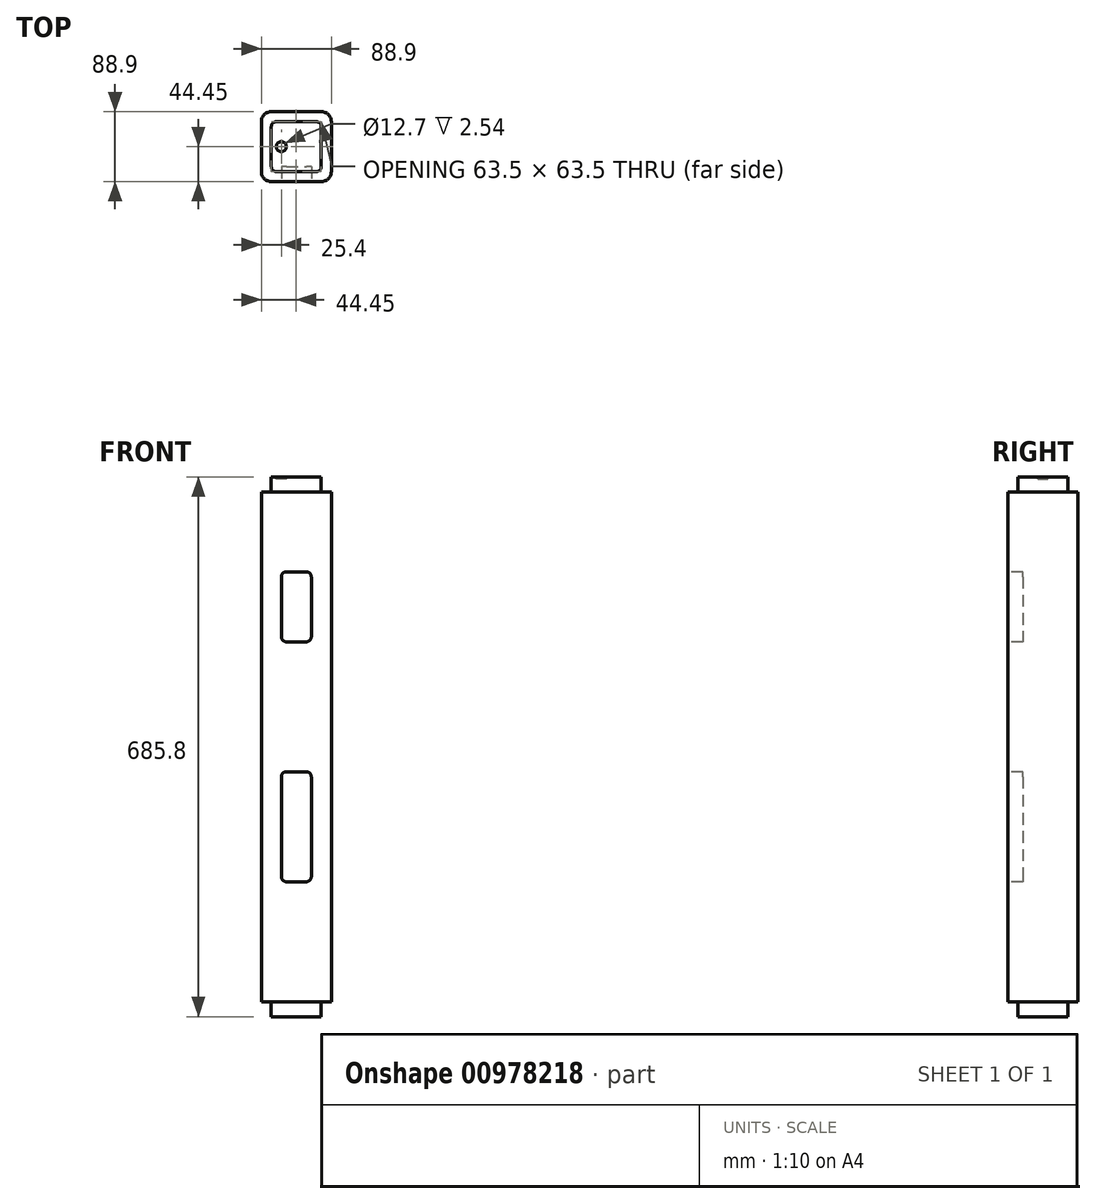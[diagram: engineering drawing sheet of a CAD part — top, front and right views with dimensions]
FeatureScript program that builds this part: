
annotation { "Feature Type Name" : "Feature", "Feature Type Description" : "" }
export const myFeature = defineFeature(function(context is Context, id is Id, definition is map)
    precondition{}
    {
        {
            var Q0;
            Q0=qCreatedBy(makeId("Front.planeOp"),FACE);
            var sketch = newSketch(context, id + "F0", { "sketchPlane" : qUnion([Q0])});
            skLineSegment(sketch, "E0", {"start": v(0, 0) * mm, "end": v(0, 101.9) * mm, "construction": true});
            skSolve(sketch);
        }
        {
            var Q0;
            Q0=qCreatedBy(makeId("Top.planeOp"),FACE);
            var sketch = newSketch(context, id + "F1", { "sketchPlane" : qUnion([Q0])});
            skLineSegment(sketch, "E1", {"start": v(0, 0) * mm, "end": v(0, 44.45) * mm, "construction": true});
            skLineSegment(sketch, "E2", {"start": v(0, 0) * mm, "end": v(-44.45, 0) * mm, "construction": true});
            skLineSegment(sketch, "E3", {"start": v(0, 0) * mm, "end": v(0, -44.45) * mm, "construction": true});
            skLineSegment(sketch, "E4", {"start": v(0, 0) * mm, "end": v(44.45, 0) * mm, "construction": true});
            skLineSegment(sketch, "E5", {"start": v(-44.45, 0) * mm, "end": v(-44.45, 19.05) * mm});
            skLineSegment(sketch, "E6", {"start": v(-44.45, 19.05) * mm, "end": v(-19.05, 19.05) * mm, "construction": true});
            skLineSegment(sketch, "E7", {"start": v(-19.05, 19.05) * mm, "end": v(-19.05, 44.45) * mm, "construction": true});
            skLineSegment(sketch, "E8", {"start": v(0, 44.45) * mm, "end": v(-19.05, 44.45) * mm});
            skLineSegment(sketch, "E9", {"start": v(-44.45, 0) * mm, "end": v(-44.45, -19.05) * mm});
            skLineSegment(sketch, "E10", {"start": v(-44.45, -19.05) * mm, "end": v(-19.05, -19.05) * mm, "construction": true});
            skLineSegment(sketch, "E11", {"start": v(-19.05, -19.05) * mm, "end": v(-19.05, -44.45) * mm, "construction": true});
            skLineSegment(sketch, "E12", {"start": v(-19.05, -44.45) * mm, "end": v(0, -44.45) * mm});
            skLineSegment(sketch, "E13", {"start": v(0, 44.45) * mm, "end": v(19.05, 44.45) * mm});
            skLineSegment(sketch, "E14", {"start": v(19.05, 44.45) * mm, "end": v(19.05, 19.05) * mm, "construction": true});
            skLineSegment(sketch, "E15", {"start": v(19.05, 19.05) * mm, "end": v(44.45, 19.05) * mm, "construction": true});
            skLineSegment(sketch, "E16", {"start": v(44.45, 0) * mm, "end": v(44.45, 19.05) * mm});
            skLineSegment(sketch, "E17", {"start": v(44.45, 0) * mm, "end": v(44.45, -19.05) * mm});
            skLineSegment(sketch, "E18", {"start": v(44.45, -19.05) * mm, "end": v(19.05, -19.05) * mm, "construction": true});
            skLineSegment(sketch, "E19", {"start": v(19.05, -19.05) * mm, "end": v(19.05, -44.45) * mm, "construction": true});
            skLineSegment(sketch, "E20", {"start": v(0, -44.45) * mm, "end": v(19.05, -44.45) * mm});
            skLineSegment(sketch, "E21", {"start": v(44.45, -19.05) * mm, "end": v(44.45, -44.45) * mm});
            skLineSegment(sketch, "E22", {"start": v(19.05, -44.45) * mm, "end": v(44.45, -44.45) * mm});
            skLineSegment(sketch, "E23", {"start": v(-19.05, -44.45) * mm, "end": v(-44.45, -44.45) * mm});
            skLineSegment(sketch, "E24", {"start": v(-44.45, -19.05) * mm, "end": v(-44.45, -44.45) * mm});
            skLineSegment(sketch, "E25", {"start": v(44.45, 19.05) * mm, "end": v(44.45, 44.45) * mm});
            skLineSegment(sketch, "E26", {"start": v(19.05, 44.45) * mm, "end": v(44.45, 44.45) * mm});
            skLineSegment(sketch, "E27", {"start": v(-19.05, 44.45) * mm, "end": v(-44.45, 44.45) * mm});
            skLineSegment(sketch, "E28", {"start": v(-44.45, 19.05) * mm, "end": v(-44.45, 44.45) * mm});
            skSolve(sketch);
        }
        {
            var Q0;
            Q0=makeQuery(id+"F1.imprint","IMPRINT",FACE,{"disambiguationData":[TD([[makeQuery(id+"F1.imprint","IMPRINT",EDGE,{"derivedFrom":sQuery(id+"F1.wireOp",EDGE,"E5")}),-1.0]])]});
            extrude(context, id + "F2", {"entities" : qUnion([Q0]), "oppositeDirection" : true, "depth" : 647.7 * mm, "offsetDistance" : 25.4 * mm});
        }
        {
            var Q0;
            Q0=makeQuery(id+"F2.opExtrude","SWEPT_FACE",FACE,{"disambiguationData":[OSD([sQuery(id+"F1.wireOp",EDGE,"E12"),sQuery(id+"F1.wireOp",EDGE,"E20")])]});
            var sketch = newSketch(context, id + "F3", { "sketchPlane" : qUnion([Q0])});
            skLineSegment(sketch, "E29.bottom", {"start": v(-19.05, -101.6) * mm, "end": v(19.05, -101.6) * mm});
            skLineSegment(sketch, "E29.top", {"start": v(-19.05, -190.5) * mm, "end": v(19.05, -190.5) * mm});
            skLineSegment(sketch, "E29.left", {"start": v(-19.05, -101.6) * mm, "end": v(-19.05, -190.5) * mm});
            skLineSegment(sketch, "E29.right", {"start": v(19.05, -101.6) * mm, "end": v(19.05, -190.5) * mm});
            skLineSegment(sketch, "E30", {"start": v(0, -190.5) * mm, "end": v(0, -647.7) * mm});
            skSolve(sketch);
        }
        {
            var Q0;
            Q0=makeQuery(id+"F3.imprint","IMPRINT",FACE,{"disambiguationData":[TD([[makeQuery(id+"F3.imprint","IMPRINT",EDGE,{"derivedFrom":sQuery(id+"F3.wireOp",EDGE,"E29.bottom")}),-1.0]])]});
            extrude(context, id + "F4", {"entities" : qUnion([Q0]), "operationType" : NewBodyOperationType.REMOVE, "oppositeDirection" : true, "depth" : 19.05 * mm, "offsetDistance" : 25.4 * mm});
        }
        {
            var Q0;
            Q0=makeQuery(id+"F2.opExtrude","SWEPT_EDGE",EDGE,{"disambiguationData":[OSD([sQuery(id+"F1.wireOp",EDGE,"E23"),sQuery(id+"F1.wireOp",EDGE,"E24")])]});
            var Q1;
            Q1=makeQuery(id+"F2.opExtrude","SWEPT_EDGE",EDGE,{"disambiguationData":[OSD([sQuery(id+"F1.wireOp",EDGE,"E21"),sQuery(id+"F1.wireOp",EDGE,"E22")])]});
            var Q2;
            Q2=makeQuery(id+"F2.opExtrude","SWEPT_EDGE",EDGE,{"disambiguationData":[OSD([sQuery(id+"F1.wireOp",EDGE,"E25"),sQuery(id+"F1.wireOp",EDGE,"E26")])]});
            var Q3;
            Q3=makeQuery(id+"F2.opExtrude","SWEPT_EDGE",EDGE,{"disambiguationData":[OSD([sQuery(id+"F1.wireOp",EDGE,"E27"),sQuery(id+"F1.wireOp",EDGE,"E28")])]});
            fillet(context, id + "F5", {"entities" : qUnion([Q0, Q1, Q2, Q3]), "radius" : 12.7 * mm, "tangentPropagation" : true, "allowEdgeOverflow" : false});
        }
        {
            var Q0;
            Q0=makeQuery(id+"FQYmMgn2PXSCWJs_1.2.F4.boolean.opBoolean","COPY",EDGE,{"derivedFrom":makeQuery(id+"FQYmMgn2PXSCWJs_1.2.F4.opExtrude","SWEPT_EDGE",EDGE,{"disambiguationData":[OSD([sQuery(id+"F3.wireOp",EDGE,"E29.top"),sQuery(id+"F3.wireOp",EDGE,"E29.right")])]})});
            var Q1;
            Q1=makeQuery(id+"FQYmMgn2PXSCWJs_1.2.F4.boolean.opBoolean","COPY",EDGE,{"derivedFrom":makeQuery(id+"FQYmMgn2PXSCWJs_1.2.F4.opExtrude","SWEPT_EDGE",EDGE,{"disambiguationData":[OSD([sQuery(id+"F3.wireOp",EDGE,"E29.top"),sQuery(id+"F3.wireOp",EDGE,"E29.left")])]})});
            var Q2;
            Q2=makeQuery(id+"FQYmMgn2PXSCWJs_1.3.F4.boolean.opBoolean","COPY",EDGE,{"derivedFrom":makeQuery(id+"FQYmMgn2PXSCWJs_1.3.F4.opExtrude","SWEPT_EDGE",EDGE,{"disambiguationData":[OSD([sQuery(id+"F3.wireOp",EDGE,"E29.top"),sQuery(id+"F3.wireOp",EDGE,"E29.left")])]})});
            var Q3;
            Q3=makeQuery(id+"FQYmMgn2PXSCWJs_1.3.F4.boolean.opBoolean","COPY",EDGE,{"derivedFrom":makeQuery(id+"FQYmMgn2PXSCWJs_1.3.F4.opExtrude","SWEPT_EDGE",EDGE,{"disambiguationData":[OSD([sQuery(id+"F3.wireOp",EDGE,"E29.top"),sQuery(id+"F3.wireOp",EDGE,"E29.right")])]})});
            var Q4;
            Q4=makeQuery(id+"F4.boolean.opBoolean","COPY",EDGE,{"derivedFrom":makeQuery(id+"F4.opExtrude","SWEPT_EDGE",EDGE,{"disambiguationData":[OSD([sQuery(id+"F3.wireOp",EDGE,"E29.top"),sQuery(id+"F3.wireOp",EDGE,"E29.left")])]})});
            var Q5;
            Q5=makeQuery(id+"F4.boolean.opBoolean","COPY",EDGE,{"derivedFrom":makeQuery(id+"F4.opExtrude","SWEPT_EDGE",EDGE,{"disambiguationData":[OSD([sQuery(id+"F3.wireOp",EDGE,"E29.top"),sQuery(id+"F3.wireOp",EDGE,"E29.right")])]})});
            var Q6;
            Q6=makeQuery(id+"FQYmMgn2PXSCWJs_1.1.F4.boolean.opBoolean","COPY",EDGE,{"derivedFrom":makeQuery(id+"FQYmMgn2PXSCWJs_1.1.F4.opExtrude","SWEPT_EDGE",EDGE,{"disambiguationData":[OSD([sQuery(id+"F3.wireOp",EDGE,"E29.top"),sQuery(id+"F3.wireOp",EDGE,"E29.right")])]})});
            var Q7;
            Q7=makeQuery(id+"FQYmMgn2PXSCWJs_1.1.F4.boolean.opBoolean","COPY",EDGE,{"derivedFrom":makeQuery(id+"FQYmMgn2PXSCWJs_1.1.F4.opExtrude","SWEPT_EDGE",EDGE,{"disambiguationData":[OSD([sQuery(id+"F3.wireOp",EDGE,"E29.top"),sQuery(id+"F3.wireOp",EDGE,"E29.left")])]})});
            var Q8;
            Q8=makeQuery(id+"FQYmMgn2PXSCWJs_1.3.F4.boolean.opBoolean","COPY",EDGE,{"derivedFrom":makeQuery(id+"FQYmMgn2PXSCWJs_1.3.F4.opExtrude","SWEPT_EDGE",EDGE,{"disambiguationData":[OSD([sQuery(id+"F3.wireOp",EDGE,"E29.bottom"),sQuery(id+"F3.wireOp",EDGE,"E29.left")])]})});
            var Q9;
            Q9=makeQuery(id+"FQYmMgn2PXSCWJs_1.3.F4.boolean.opBoolean","COPY",EDGE,{"derivedFrom":makeQuery(id+"FQYmMgn2PXSCWJs_1.3.F4.opExtrude","SWEPT_EDGE",EDGE,{"disambiguationData":[OSD([sQuery(id+"F3.wireOp",EDGE,"E29.bottom"),sQuery(id+"F3.wireOp",EDGE,"E29.right")])]})});
            var Q10;
            Q10=makeQuery(id+"FQYmMgn2PXSCWJs_1.2.F4.boolean.opBoolean","COPY",EDGE,{"derivedFrom":makeQuery(id+"FQYmMgn2PXSCWJs_1.2.F4.opExtrude","SWEPT_EDGE",EDGE,{"disambiguationData":[OSD([sQuery(id+"F3.wireOp",EDGE,"E29.bottom"),sQuery(id+"F3.wireOp",EDGE,"E29.left")])]})});
            var Q11;
            Q11=makeQuery(id+"FQYmMgn2PXSCWJs_1.2.F4.boolean.opBoolean","COPY",EDGE,{"derivedFrom":makeQuery(id+"FQYmMgn2PXSCWJs_1.2.F4.opExtrude","SWEPT_EDGE",EDGE,{"disambiguationData":[OSD([sQuery(id+"F3.wireOp",EDGE,"E29.bottom"),sQuery(id+"F3.wireOp",EDGE,"E29.right")])]})});
            var Q12;
            Q12=makeQuery(id+"FQYmMgn2PXSCWJs_1.1.F4.boolean.opBoolean","COPY",EDGE,{"derivedFrom":makeQuery(id+"FQYmMgn2PXSCWJs_1.1.F4.opExtrude","SWEPT_EDGE",EDGE,{"disambiguationData":[OSD([sQuery(id+"F3.wireOp",EDGE,"E29.bottom"),sQuery(id+"F3.wireOp",EDGE,"E29.left")])]})});
            var Q13;
            Q13=makeQuery(id+"FQYmMgn2PXSCWJs_1.1.F4.boolean.opBoolean","COPY",EDGE,{"derivedFrom":makeQuery(id+"FQYmMgn2PXSCWJs_1.1.F4.opExtrude","SWEPT_EDGE",EDGE,{"disambiguationData":[OSD([sQuery(id+"F3.wireOp",EDGE,"E29.bottom"),sQuery(id+"F3.wireOp",EDGE,"E29.right")])]})});
            var Q14;
            Q14=makeQuery(id+"F4.boolean.opBoolean","COPY",EDGE,{"derivedFrom":makeQuery(id+"F4.opExtrude","SWEPT_EDGE",EDGE,{"disambiguationData":[OSD([sQuery(id+"F3.wireOp",EDGE,"E29.bottom"),sQuery(id+"F3.wireOp",EDGE,"E29.left")])]})});
            var Q15;
            Q15=makeQuery(id+"F4.boolean.opBoolean","COPY",EDGE,{"derivedFrom":makeQuery(id+"F4.opExtrude","SWEPT_EDGE",EDGE,{"disambiguationData":[OSD([sQuery(id+"F3.wireOp",EDGE,"E29.bottom"),sQuery(id+"F3.wireOp",EDGE,"E29.right")])]})});
            fillet(context, id + "F6", {"entities" : qUnion([Q0, Q1, Q2, Q3, Q4, Q5, Q6, Q7, Q8, Q9, Q10, Q11, Q12, Q13, Q14, Q15]), "radius" : 6.35 * mm, "tangentPropagation" : true, "allowEdgeOverflow" : false});
        }
        {
            var Q0;
            Q0=makeQuery(id+"F2.opExtrude","SWEPT_FACE",FACE,{"disambiguationData":[OSD([sQuery(id+"F1.wireOp",EDGE,"E12"),sQuery(id+"F1.wireOp",EDGE,"E20"),sQuery(id+"F1.wireOp",EDGE,"E22"),sQuery(id+"F1.wireOp",EDGE,"E23")])]});
            var sketch = newSketch(context, id + "F7", { "sketchPlane" : qUnion([Q0])});
            skLineSegment(sketch, "E31.bottom", {"start": v(-19.05, -355.6) * mm, "end": v(19.05, -355.6) * mm});
            skLineSegment(sketch, "E31.top", {"start": v(-19.05, -495.3) * mm, "end": v(19.05, -495.3) * mm});
            skLineSegment(sketch, "E31.left", {"start": v(-19.05, -355.6) * mm, "end": v(-19.05, -495.3) * mm});
            skLineSegment(sketch, "E31.right", {"start": v(19.05, -355.6) * mm, "end": v(19.05, -495.3) * mm});
            skLineSegment(sketch, "E32", {"start": v(0, -495.3) * mm, "end": v(0, -647.7) * mm, "construction": true});
            skSolve(sketch);
        }
        {
            var Q0;
            Q0=makeQuery(id+"F7.imprint","IMPRINT",FACE,{"disambiguationData":[TD([[makeQuery(id+"F7.imprint","IMPRINT",EDGE,{"derivedFrom":sQuery(id+"F7.wireOp",EDGE,"E31.bottom")}),-1.0]])]});
            extrude(context, id + "F8", {"entities" : qUnion([Q0]), "operationType" : NewBodyOperationType.REMOVE, "oppositeDirection" : true, "depth" : 19.05 * mm, "offsetDistance" : 25.4 * mm});
        }
        {
            var Q0;
            Q0=makeQuery(id+"F8.boolean.opBoolean","COPY",EDGE,{"derivedFrom":makeQuery(id+"F8.opExtrude","SWEPT_EDGE",EDGE,{"disambiguationData":[OSD([sQuery(id+"F7.wireOp",EDGE,"E31.bottom"),sQuery(id+"F7.wireOp",EDGE,"E31.left")])]})});
            var Q1;
            Q1=makeQuery(id+"F8.boolean.opBoolean","COPY",EDGE,{"derivedFrom":makeQuery(id+"F8.opExtrude","SWEPT_EDGE",EDGE,{"disambiguationData":[OSD([sQuery(id+"F7.wireOp",EDGE,"E31.bottom"),sQuery(id+"F7.wireOp",EDGE,"E31.right")])]})});
            var Q2;
            Q2=makeQuery(id+"F8.boolean.opBoolean","COPY",EDGE,{"derivedFrom":makeQuery(id+"F8.opExtrude","SWEPT_EDGE",EDGE,{"disambiguationData":[OSD([sQuery(id+"F7.wireOp",EDGE,"E31.top"),sQuery(id+"F7.wireOp",EDGE,"E31.right")])]})});
            var Q3;
            Q3=makeQuery(id+"F8.boolean.opBoolean","COPY",EDGE,{"derivedFrom":makeQuery(id+"F8.opExtrude","SWEPT_EDGE",EDGE,{"disambiguationData":[OSD([sQuery(id+"F7.wireOp",EDGE,"E31.top"),sQuery(id+"F7.wireOp",EDGE,"E31.left")])]})});
            fillet(context, id + "F9", {"entities" : qUnion([Q0, Q1, Q2, Q3]), "radius" : 6.35 * mm, "tangentPropagation" : true, "allowEdgeOverflow" : false});
        }
        {
            var Q0;
            Q0=makeQuery(id+"F2.opExtrude","CAP_FACE",FACE,{"disambiguationData":[OSD([sQuery(id+"F1.wireOp",EDGE,"E5"),sQuery(id+"F1.wireOp",EDGE,"E8"),sQuery(id+"F1.wireOp",EDGE,"E9"),sQuery(id+"F1.wireOp",EDGE,"E12"),sQuery(id+"F1.wireOp",EDGE,"E13"),sQuery(id+"F1.wireOp",EDGE,"E16"),sQuery(id+"F1.wireOp",EDGE,"E17"),sQuery(id+"F1.wireOp",EDGE,"E20"),sQuery(id+"F1.wireOp",EDGE,"E21"),sQuery(id+"F1.wireOp",EDGE,"E22"),sQuery(id+"F1.wireOp",EDGE,"E23"),sQuery(id+"F1.wireOp",EDGE,"E24"),sQuery(id+"F1.wireOp",EDGE,"E25"),sQuery(id+"F1.wireOp",EDGE,"E26"),sQuery(id+"F1.wireOp",EDGE,"E27"),sQuery(id+"F1.wireOp",EDGE,"E28")])],"isStart":true});
            var sketch = newSketch(context, id + "F10", { "sketchPlane" : qUnion([Q0])});
            skLineSegment(sketch, "E33.bottom", {"start": v(25.4, -31.75) * mm, "end": v(-25.4, -31.75) * mm});
            skLineSegment(sketch, "E33.top", {"start": v(25.4, 31.75) * mm, "end": v(-25.4, 31.75) * mm});
            skLineSegment(sketch, "E33.left", {"start": v(31.75, -25.4) * mm, "end": v(31.75, 25.4) * mm});
            skLineSegment(sketch, "E33.right", {"start": v(-31.75, -25.4) * mm, "end": v(-31.75, 25.4) * mm});
            skPoint(sketch, "E33.middle", {"position": v(0, 0) * mm});
            skPoint(sketch, "E34.visualSharp", {"position": v(-31.75, 31.75) * mm});
            skArc(sketch, "E34.filletArc", {"start": v(-25.4, 31.75) * mm, "mid": v(-29.9, 29.9) * mm, "end": v(-31.75, 25.4) * mm});
            skPoint(sketch, "E35.visualSharp", {"position": v(31.75, 31.75) * mm});
            skArc(sketch, "E35.filletArc", {"start": v(31.75, 25.4) * mm, "mid": v(29.9, 29.9) * mm, "end": v(25.4, 31.75) * mm});
            skPoint(sketch, "E36.visualSharp", {"position": v(31.75, -31.75) * mm});
            skArc(sketch, "E36.filletArc", {"start": v(25.4, -31.75) * mm, "mid": v(29.9, -29.9) * mm, "end": v(31.75, -25.4) * mm});
            skPoint(sketch, "E37.visualSharp", {"position": v(-31.75, -31.75) * mm});
            skArc(sketch, "E37.filletArc", {"start": v(-31.75, -25.4) * mm, "mid": v(-29.9, -29.9) * mm, "end": v(-25.4, -31.75) * mm});
            skSolve(sketch);
        }
        {
            var Q0;
            Q0=makeQuery(id+"F10.imprint","IMPRINT",FACE,{"disambiguationData":[TD([[makeQuery(id+"F10.imprint","IMPRINT",EDGE,{"derivedFrom":sQuery(id+"F10.wireOp",EDGE,"E33.bottom")}),-1.0]])]});
            extrude(context, id + "F11", {"entities" : qUnion([Q0]), "operationType" : NewBodyOperationType.ADD, "depth" : 19.05 * mm, "offsetDistance" : 25.4 * mm});
        }
        {
            var Q0;
            Q0=makeQuery(id+"F2.opExtrude","CAP_FACE",FACE,{"disambiguationData":[OSD([sQuery(id+"F1.wireOp",EDGE,"E5"),sQuery(id+"F1.wireOp",EDGE,"E8"),sQuery(id+"F1.wireOp",EDGE,"E9"),sQuery(id+"F1.wireOp",EDGE,"E12"),sQuery(id+"F1.wireOp",EDGE,"E13"),sQuery(id+"F1.wireOp",EDGE,"E16"),sQuery(id+"F1.wireOp",EDGE,"E17"),sQuery(id+"F1.wireOp",EDGE,"E20"),sQuery(id+"F1.wireOp",EDGE,"E21"),sQuery(id+"F1.wireOp",EDGE,"E22"),sQuery(id+"F1.wireOp",EDGE,"E23"),sQuery(id+"F1.wireOp",EDGE,"E24"),sQuery(id+"F1.wireOp",EDGE,"E25"),sQuery(id+"F1.wireOp",EDGE,"E26"),sQuery(id+"F1.wireOp",EDGE,"E27"),sQuery(id+"F1.wireOp",EDGE,"E28")])],"isStart":false});
            var sketch = newSketch(context, id + "F12", { "sketchPlane" : qUnion([Q0])});
            skLineSegment(sketch, "E38.bottom", {"start": v(25.4, -31.75) * mm, "end": v(-25.4, -31.75) * mm});
            skLineSegment(sketch, "E38.top", {"start": v(25.4, 31.75) * mm, "end": v(-25.4, 31.75) * mm});
            skLineSegment(sketch, "E38.left", {"start": v(31.75, -25.4) * mm, "end": v(31.75, 25.4) * mm});
            skLineSegment(sketch, "E38.right", {"start": v(-31.75, -25.4) * mm, "end": v(-31.75, 25.4) * mm});
            skPoint(sketch, "E38.middle", {"position": v(0, 0) * mm});
            skPoint(sketch, "E39.visualSharp", {"position": v(-31.75, 31.75) * mm});
            skArc(sketch, "E39.filletArc", {"start": v(-25.4, 31.75) * mm, "mid": v(-29.9, 29.9) * mm, "end": v(-31.75, 25.4) * mm});
            skPoint(sketch, "E40.visualSharp", {"position": v(31.75, 31.75) * mm});
            skArc(sketch, "E40.filletArc", {"start": v(31.75, 25.4) * mm, "mid": v(29.9, 29.9) * mm, "end": v(25.4, 31.75) * mm});
            skPoint(sketch, "E41.visualSharp", {"position": v(31.75, -31.75) * mm});
            skArc(sketch, "E41.filletArc", {"start": v(25.4, -31.75) * mm, "mid": v(29.9, -29.9) * mm, "end": v(31.75, -25.4) * mm});
            skPoint(sketch, "E42.visualSharp", {"position": v(-31.75, -31.75) * mm});
            skArc(sketch, "E42.filletArc", {"start": v(-31.75, -25.4) * mm, "mid": v(-29.9, -29.9) * mm, "end": v(-25.4, -31.75) * mm});
            skSolve(sketch);
        }
        {
            var Q0;
            Q0 = qSketchRegion(id + "F12", true);
            extrude(context, id + "F13", {"entities" : qUnion([Q0]), "operationType" : NewBodyOperationType.ADD, "depth" : 19.05 * mm, "offsetDistance" : 25.4 * mm});
        }
        {
            var Q0;
            Q0=makeQuery(id+"F11.opExtrude","CAP_FACE",FACE,{"disambiguationData":[OSD([sQuery(id+"F10.wireOp",EDGE,"E33.bottom"),sQuery(id+"F10.wireOp",EDGE,"E33.top"),sQuery(id+"F10.wireOp",EDGE,"E33.left"),sQuery(id+"F10.wireOp",EDGE,"E33.right"),sQuery(id+"F10.wireOp",EDGE,"E34.filletArc"),sQuery(id+"F10.wireOp",EDGE,"E35.filletArc"),sQuery(id+"F10.wireOp",EDGE,"E36.filletArc"),sQuery(id+"F10.wireOp",EDGE,"E37.filletArc")])],"isStart":false});
            var sketch = newSketch(context, id + "F14", { "sketchPlane" : qUnion([Q0])});
            skCircle(sketch, "E43", {"center": v(-19.05, 0) * mm, "radius": 6.35 * mm});
            skSolve(sketch);
        }
        {
            var Q0;
            Q0=makeQuery(id+"F14.imprint","IMPRINT",FACE,{"disambiguationData":[TD([[makeQuery(id+"F14.imprint","IMPRINT",EDGE,{"derivedFrom":sQuery(id+"F14.wireOp",EDGE,"E43")}),1.0]])]});
            extrude(context, id + "F15", {"entities" : qUnion([Q0]), "operationType" : NewBodyOperationType.REMOVE, "oppositeDirection" : true, "depth" : 2.54 * mm, "offsetDistance" : 25.4 * mm});
        }
    });
